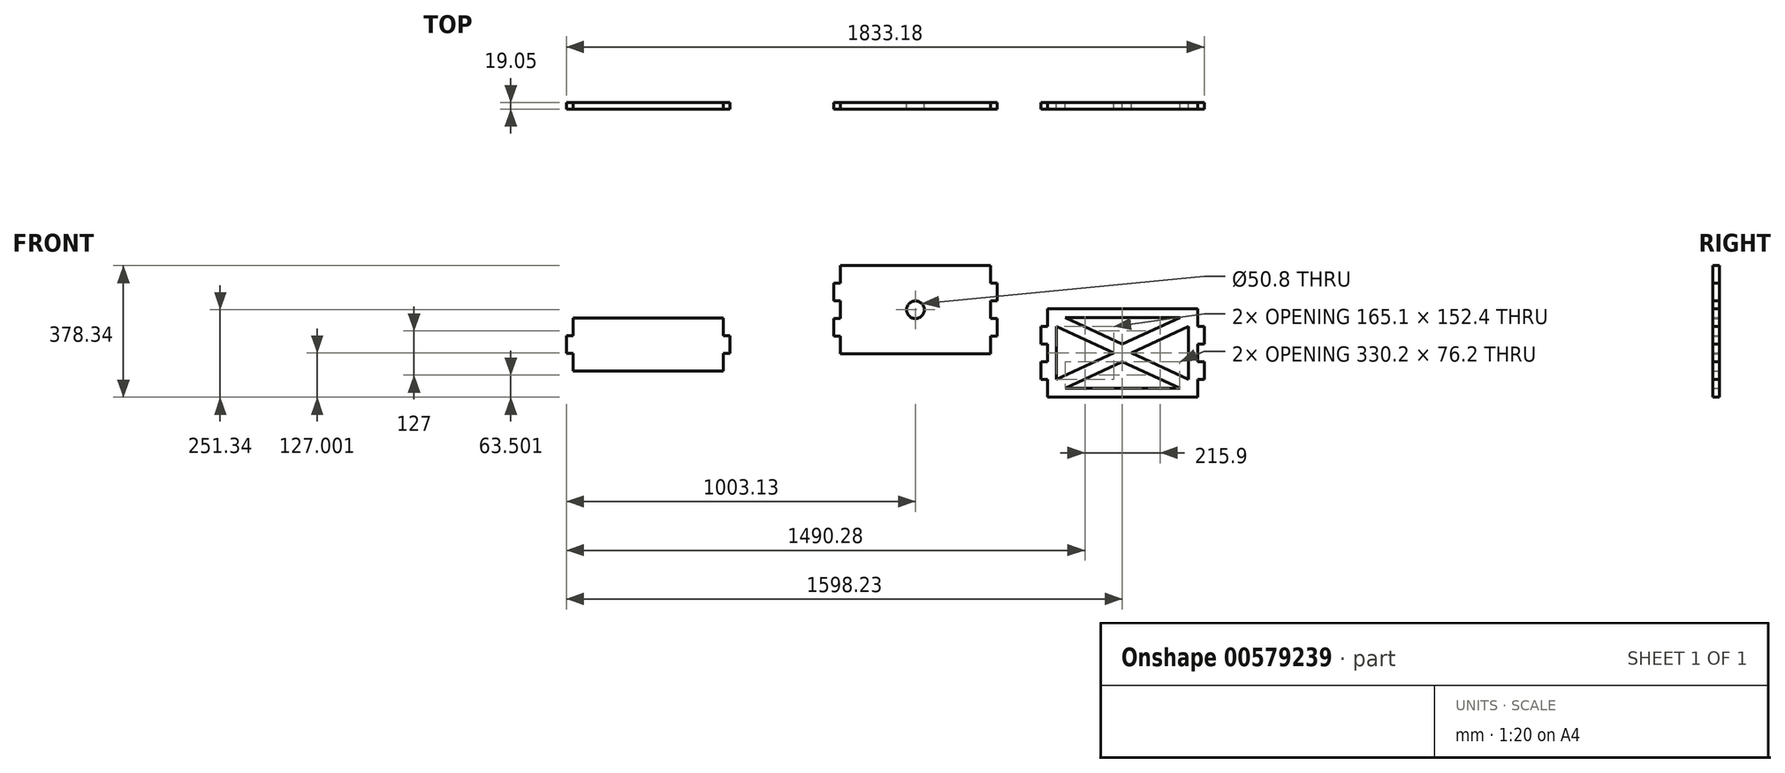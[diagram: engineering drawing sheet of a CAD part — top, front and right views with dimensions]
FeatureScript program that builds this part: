
annotation { "Feature Type Name" : "Feature", "Feature Type Description" : "" }
export const myFeature = defineFeature(function(context is Context, id is Id, definition is map)
    precondition{}
    {
        {
            var Q0;
            Q0=qCreatedBy(makeId("Front.planeOp"),FACE);
            var sketch = newSketch(context, id + "F0", { "sketchPlane" : qUnion([Q0])});
            skLineSegment(sketch, "E0.bottom", {"start": v(-383.1, 205.12) * mm, "end": v(48.7, 205.12) * mm});
            skLineSegment(sketch, "E0.top", {"start": v(-383.1, -48.88) * mm, "end": v(48.7, -48.88) * mm});
            skLineSegment(sketch, "E0.left", {"start": v(-402.16, 154.32) * mm, "end": v(-402.16, 103.52) * mm});
            skLineSegment(sketch, "E0.right", {"start": v(67.74, 154.32) * mm, "end": v(67.74, 103.52) * mm});
            skLineSegment(sketch, "E1.bottom", {"start": v(48.7, 1.92) * mm, "end": v(67.74, 1.92) * mm});
            skLineSegment(sketch, "E1.left", {"start": v(48.7, 1.92) * mm, "end": v(48.7, -48.88) * mm});
            skLineSegment(sketch, "E2.top", {"start": v(-402.16, 154.32) * mm, "end": v(-383.1, 154.32) * mm});
            skLineSegment(sketch, "E2.right", {"start": v(-383.1, 205.12) * mm, "end": v(-383.1, 154.32) * mm});
            skLineSegment(sketch, "E3.top", {"start": v(-402.16, 103.52) * mm, "end": v(-383.1, 103.52) * mm});
            skLineSegment(sketch, "E4.top", {"start": v(-402.16, 52.72) * mm, "end": v(-383.1, 52.72) * mm});
            skLineSegment(sketch, "E4.right", {"start": v(-383.1, 103.52) * mm, "end": v(-383.1, 52.72) * mm});
            skLineSegment(sketch, "E5.top", {"start": v(-402.16, 1.92) * mm, "end": v(-383.1, 1.92) * mm});
            skLineSegment(sketch, "E5.left", {"start": v(-402.16, 52.72) * mm, "end": v(-402.16, 1.92) * mm});
            skLineSegment(sketch, "E6.right", {"start": v(-383.1, 1.92) * mm, "end": v(-383.1, -48.88) * mm});
            skLineSegment(sketch, "E7.bottom", {"start": v(48.7, 52.72) * mm, "end": v(67.74, 52.72) * mm});
            skLineSegment(sketch, "E7.right", {"start": v(67.74, 52.72) * mm, "end": v(67.74, 1.92) * mm});
            skLineSegment(sketch, "E8.bottom", {"start": v(48.7, 103.52) * mm, "end": v(67.74, 103.52) * mm});
            skLineSegment(sketch, "E8.left", {"start": v(48.7, 103.52) * mm, "end": v(48.7, 52.72) * mm});
            skLineSegment(sketch, "E9.bottom", {"start": v(48.7, 154.32) * mm, "end": v(67.74, 154.32) * mm});
            skLineSegment(sketch, "E10.left", {"start": v(48.7, 205.12) * mm, "end": v(48.7, 154.32) * mm});
            skLineSegment(sketch, "E11.top", {"start": v(-1151.3, -98.2) * mm, "end": v(-719.5, -98.2) * mm});
            skLineSegment(sketch, "E12.bottom", {"start": v(-719.5, -47.4) * mm, "end": v(-700.44, -47.4) * mm});
            skLineSegment(sketch, "E12.left", {"start": v(-719.5, -47.4) * mm, "end": v(-719.5, -98.2) * mm});
            skLineSegment(sketch, "E13.top", {"start": v(-1170.34, 3.4) * mm, "end": v(-1151.3, 3.4) * mm});
            skLineSegment(sketch, "E13.right", {"start": v(-1151.3, 54.2) * mm, "end": v(-1151.3, 3.4) * mm});
            skLineSegment(sketch, "E14.top", {"start": v(-1170.34, -47.4) * mm, "end": v(-1151.3, -47.4) * mm});
            skLineSegment(sketch, "E14.left", {"start": v(-1170.34, 3.4) * mm, "end": v(-1170.34, -47.4) * mm});
            skLineSegment(sketch, "E15.right", {"start": v(-1151.3, -47.4) * mm, "end": v(-1151.3, -98.2) * mm});
            skLineSegment(sketch, "E16.bottom", {"start": v(-719.5, 3.4) * mm, "end": v(-700.44, 3.4) * mm});
            skLineSegment(sketch, "E16.right", {"start": v(-700.44, 3.4) * mm, "end": v(-700.44, -47.4) * mm});
            skLineSegment(sketch, "E17.left", {"start": v(-719.5, 54.2) * mm, "end": v(-719.5, 3.4) * mm});
            skLineSegment(sketch, "E18", {"start": v(-1151.3, 54.2) * mm, "end": v(-719.5, 54.2) * mm});
            skCircle(sketch, "E19", {"center": v(-167.2, 78.12) * mm, "radius": 25.4 * mm});
            skLineSegment(sketch, "E20.bottom", {"start": v(211.99, 80.78) * mm, "end": v(643.79, 80.78) * mm});
            skLineSegment(sketch, "E20.top", {"start": v(211.99, -173.22) * mm, "end": v(643.79, -173.22) * mm});
            skLineSegment(sketch, "E20.left", {"start": v(192.94, 29.98) * mm, "end": v(192.94, -20.82) * mm});
            skLineSegment(sketch, "E20.right", {"start": v(662.84, 29.98) * mm, "end": v(662.84, -20.82) * mm});
            skLineSegment(sketch, "E21.bottom", {"start": v(643.79, -122.42) * mm, "end": v(662.84, -122.42) * mm});
            skLineSegment(sketch, "E21.left", {"start": v(643.79, -122.42) * mm, "end": v(643.79, -173.22) * mm});
            skLineSegment(sketch, "E22.top", {"start": v(192.94, 29.98) * mm, "end": v(211.99, 29.98) * mm});
            skLineSegment(sketch, "E22.right", {"start": v(211.99, 80.78) * mm, "end": v(211.99, 29.98) * mm});
            skLineSegment(sketch, "E23.top", {"start": v(192.94, -20.82) * mm, "end": v(211.99, -20.82) * mm});
            skLineSegment(sketch, "E24.top", {"start": v(192.94, -71.62) * mm, "end": v(211.99, -71.62) * mm});
            skLineSegment(sketch, "E24.right", {"start": v(211.99, -20.82) * mm, "end": v(211.99, -71.62) * mm});
            skLineSegment(sketch, "E25.top", {"start": v(192.94, -122.42) * mm, "end": v(211.99, -122.42) * mm});
            skLineSegment(sketch, "E25.left", {"start": v(192.94, -71.62) * mm, "end": v(192.94, -122.42) * mm});
            skLineSegment(sketch, "E26.right", {"start": v(211.99, -122.42) * mm, "end": v(211.99, -173.22) * mm});
            skLineSegment(sketch, "E27.bottom", {"start": v(643.79, -71.62) * mm, "end": v(662.84, -71.62) * mm});
            skLineSegment(sketch, "E27.right", {"start": v(662.84, -71.62) * mm, "end": v(662.84, -122.42) * mm});
            skLineSegment(sketch, "E28.bottom", {"start": v(643.79, -20.82) * mm, "end": v(662.84, -20.82) * mm});
            skLineSegment(sketch, "E28.left", {"start": v(643.79, -20.82) * mm, "end": v(643.79, -71.62) * mm});
            skLineSegment(sketch, "E29.bottom", {"start": v(643.79, 29.98) * mm, "end": v(662.84, 29.98) * mm});
            skLineSegment(sketch, "E30.left", {"start": v(643.79, 80.78) * mm, "end": v(643.79, 29.98) * mm});
            skLineSegment(sketch, "E31", {"start": v(427.89, -46.22) * mm, "end": v(402.49, -46.22) * mm});
            skLineSegment(sketch, "E32", {"start": v(402.49, -46.22) * mm, "end": v(453.29, -46.22) * mm});
            skLineSegment(sketch, "E33", {"start": v(237.39, 29.98) * mm, "end": v(237.39, -122.42) * mm});
            skLineSegment(sketch, "E34", {"start": v(618.39, 29.98) * mm, "end": v(453.29, -46.22) * mm});
            skLineSegment(sketch, "E35", {"start": v(618.39, -122.42) * mm, "end": v(453.29, -46.22) * mm});
            skLineSegment(sketch, "E36", {"start": v(618.39, 29.98) * mm, "end": v(618.39, -122.42) * mm});
            skLineSegment(sketch, "E37", {"start": v(427.89, -46.22) * mm, "end": v(427.89, -20.82) * mm});
            skLineSegment(sketch, "E38", {"start": v(427.89, -20.82) * mm, "end": v(427.89, -71.62) * mm});
            skLineSegment(sketch, "E39", {"start": v(237.39, 29.98) * mm, "end": v(402.49, -46.22) * mm});
            skLineSegment(sketch, "E40", {"start": v(402.49, -46.22) * mm, "end": v(237.39, -122.42) * mm});
            skLineSegment(sketch, "E41", {"start": v(592.99, -147.82) * mm, "end": v(427.89, -71.62) * mm});
            skLineSegment(sketch, "E42", {"start": v(262.79, -147.82) * mm, "end": v(427.89, -71.62) * mm});
            skLineSegment(sketch, "E43", {"start": v(262.79, -147.82) * mm, "end": v(592.99, -147.82) * mm});
            skLineSegment(sketch, "E44", {"start": v(262.79, 55.38) * mm, "end": v(427.89, -20.82) * mm});
            skLineSegment(sketch, "E45", {"start": v(592.99, 55.38) * mm, "end": v(427.89, -20.82) * mm});
            skLineSegment(sketch, "E46", {"start": v(262.79, 55.38) * mm, "end": v(592.99, 55.38) * mm});
            skSolve(sketch);
        }
        {
            var Q0;
            Q0=makeQuery(id+"F0.imprint","IMPRINT",FACE,{"disambiguationData":[TD([[makeQuery(id+"F0.imprint","IMPRINT",EDGE,{"derivedFrom":sQuery(id+"F0.wireOp",EDGE,"E0.bottom")}),-1.0]])]});
            extrude(context, id + "F1", {"entities" : qUnion([Q0]), "depth" : 19.05 * mm, "offsetDistance" : 25.4 * mm});
        }
        {
            var Q0;
            Q0 = qSketchRegion(id + "F0", true);
            extrude(context, id + "F2", {"entities" : qUnion([Q0]), "operationType" : NewBodyOperationType.ADD, "depth" : 19.05 * mm, "offsetDistance" : 25.4 * mm});
        }
    });
